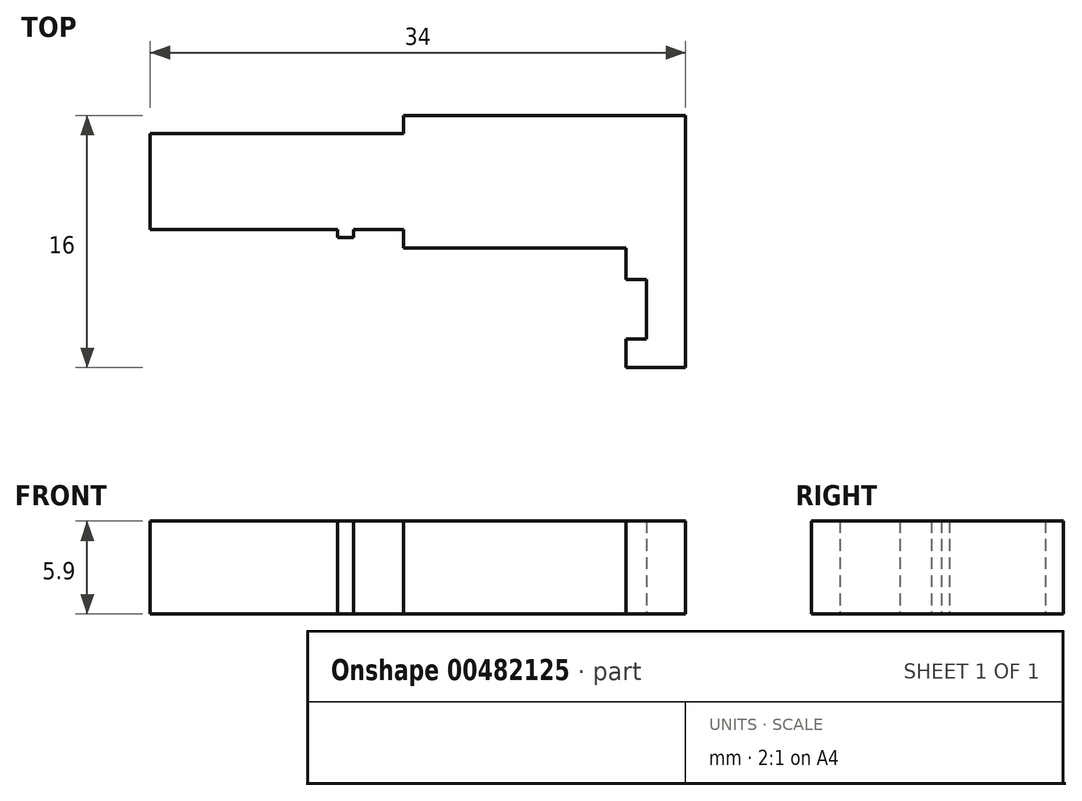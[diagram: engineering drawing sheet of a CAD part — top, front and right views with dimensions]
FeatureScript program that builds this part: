
annotation { "Feature Type Name" : "Feature", "Feature Type Description" : "" }
export const myFeature = defineFeature(function(context is Context, id is Id, definition is map)
    precondition{}
    {
        {
            var Q0;
            Q0=qCreatedBy(makeId("Top.planeOp"),FACE);
            var sketch = newSketch(context, id + "F0", { "sketchPlane" : qUnion([Q0])});
            skLineSegment(sketch, "E0", {"start": v(0, 4.2) * mm, "end": v(0, 3.05) * mm});
            skLineSegment(sketch, "E1", {"start": v(0, 3.05) * mm, "end": v(-16.1, 3.05) * mm});
            skLineSegment(sketch, "E2", {"start": v(-16.1, 3.05) * mm, "end": v(-16.1, -3.05) * mm});
            skLineSegment(sketch, "E3", {"start": v(-16.1, -3.05) * mm, "end": v(-4.2, -3.05) * mm});
            skLineSegment(sketch, "E4", {"start": v(0, -3.05) * mm, "end": v(0, -4.2) * mm});
            skLineSegment(sketch, "E5", {"start": v(0, -4.2) * mm, "end": v(14.1, -4.2) * mm});
            skLineSegment(sketch, "E6", {"start": v(14.1, -4.2) * mm, "end": v(14.1, -6.2) * mm});
            skLineSegment(sketch, "E7", {"start": v(14.1, -6.2) * mm, "end": v(15.4, -6.2) * mm});
            skLineSegment(sketch, "E8", {"start": v(15.4, -6.2) * mm, "end": v(15.4, -10) * mm});
            skLineSegment(sketch, "E9", {"start": v(15.4, -10) * mm, "end": v(14.1, -10) * mm});
            skLineSegment(sketch, "E10", {"start": v(14.1, -11.8) * mm, "end": v(14.1, -10) * mm});
            skLineSegment(sketch, "E11", {"start": v(17.9, -11.8) * mm, "end": v(14.1, -11.8) * mm});
            skLineSegment(sketch, "E12", {"start": v(17.9, -11.8) * mm, "end": v(17.9, 4.2) * mm});
            skLineSegment(sketch, "E13", {"start": v(0, 4.2) * mm, "end": v(17.9, 4.2) * mm});
            skLineSegment(sketch, "E14", {"start": v(-35.63, 0) * mm, "end": v(8.82, 0) * mm, "construction": true});
            skLineSegment(sketch, "E15.top", {"start": v(-4.2, -3.55) * mm, "end": v(-3.2, -3.55) * mm});
            skLineSegment(sketch, "E15.left", {"start": v(-4.2, -3.05) * mm, "end": v(-4.2, -3.55) * mm});
            skLineSegment(sketch, "E15.right", {"start": v(-3.2, -3.05) * mm, "end": v(-3.2, -3.55) * mm});
            skLineSegment(sketch, "E16.trimOffspring", {"start": v(-3.2, -3.05) * mm, "end": v(0, -3.05) * mm});
            skSolve(sketch);
        }
        {
            var Q0;
            Q0 = qSketchRegion(id + "F0", true);
            extrude(context, id + "F1", {"entities" : qUnion([Q0]), "depth" : 5.9 * mm});
        }
    });
